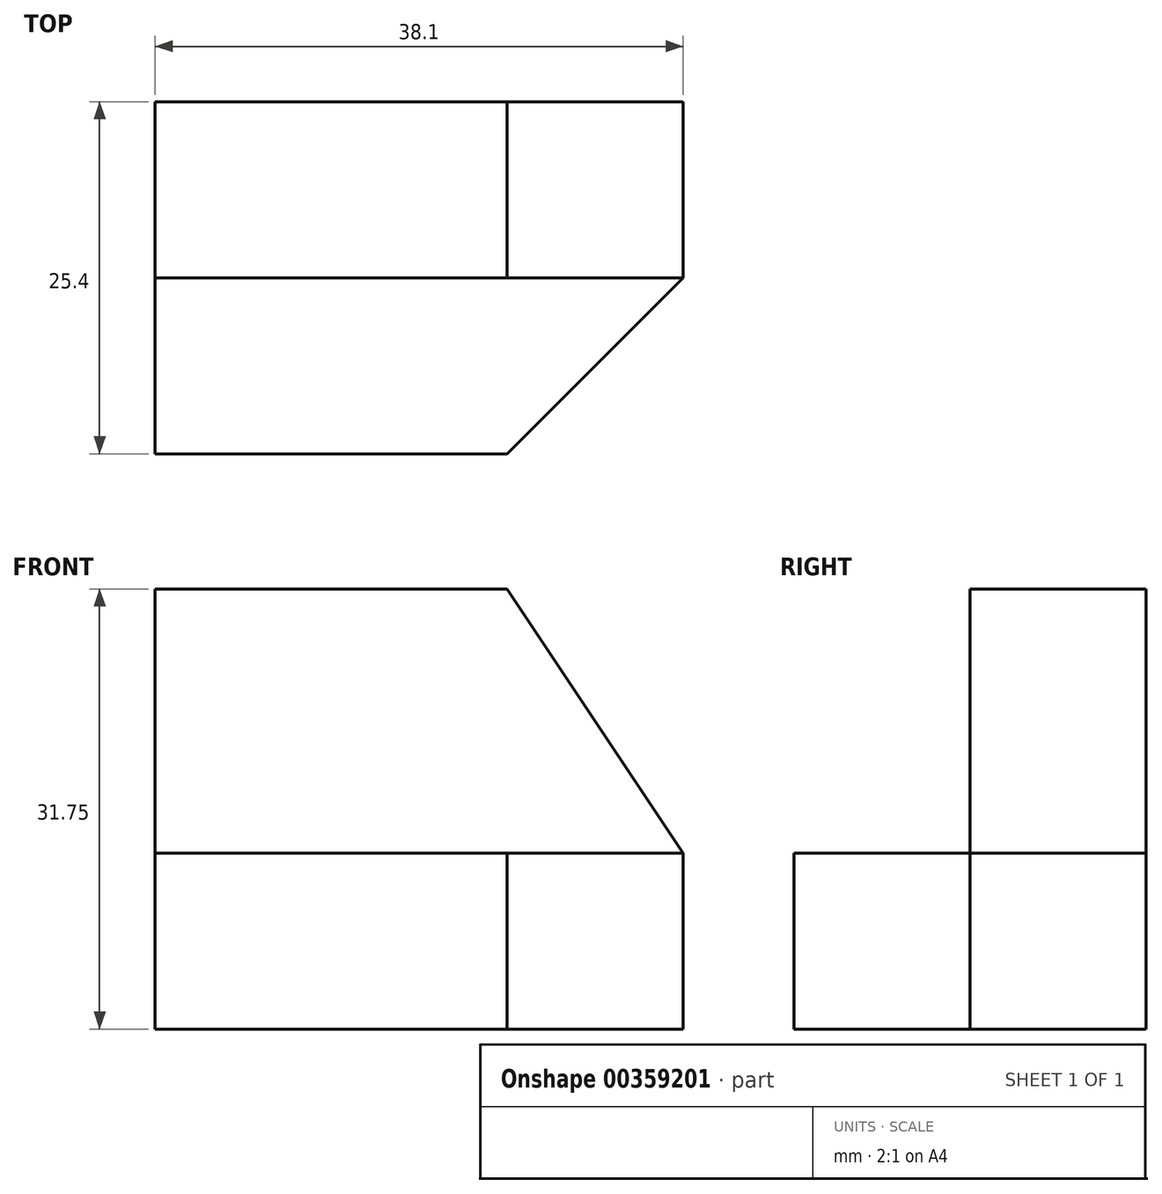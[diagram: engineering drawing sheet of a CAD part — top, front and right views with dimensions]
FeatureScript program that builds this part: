
annotation { "Feature Type Name" : "Feature", "Feature Type Description" : "" }
export const myFeature = defineFeature(function(context is Context, id is Id, definition is map)
    precondition{}
    {
        {
            var Q0;
            Q0=qCreatedBy(makeId("Right.planeOp"),FACE);
            var sketch = newSketch(context, id + "F0", { "sketchPlane" : qUnion([Q0])});
            skLineSegment(sketch, "E0", {"start": v(0, 0) * mm, "end": v(0, 12.7) * mm});
            skLineSegment(sketch, "E1", {"start": v(0, 12.7) * mm, "end": v(12.7, 12.7) * mm});
            skLineSegment(sketch, "E2", {"start": v(12.7, 12.7) * mm, "end": v(12.7, 31.75) * mm});
            skLineSegment(sketch, "E3", {"start": v(12.7, 31.75) * mm, "end": v(25.4, 31.75) * mm});
            skLineSegment(sketch, "E4", {"start": v(25.4, 31.75) * mm, "end": v(25.4, 0) * mm});
            skLineSegment(sketch, "E5", {"start": v(25.4, 0) * mm, "end": v(0, 0) * mm});
            skSolve(sketch);
        }
        {
            var Q0;
            Q0 = qSketchRegion(id + "F0", true);
            extrude(context, id + "F1", {"entities" : qUnion([Q0]), "oppositeDirection" : true, "depth" : 38.1 * mm});
        }
        {
            var Q0;
            Q0=makeQuery(id+"F1.opExtrude","SWEPT_FACE",FACE,{"disambiguationData":[OSD([sQuery(id+"F0.wireOp",EDGE,"E2")])]});
            var sketch = newSketch(context, id + "F2", { "sketchPlane" : qUnion([Q0])});
            skLineSegment(sketch, "E6", {"start": v(-12.7, 31.75) * mm, "end": v(0, 12.7) * mm});
            skLineSegment(sketch, "E7", {"start": v(0, 12.7) * mm, "end": v(0, 31.75) * mm});
            skLineSegment(sketch, "E8", {"start": v(0, 31.75) * mm, "end": v(-12.7, 31.75) * mm});
            skSolve(sketch);
        }
        {
            var Q0;
            Q0 = qSketchRegion(id + "F2", true);
            extrude(context, id + "F3", {"entities" : qUnion([Q0]), "operationType" : NewBodyOperationType.REMOVE, "oppositeDirection" : true, "depth" : 25.4 * mm});
        }
        {
            var Q0;
            Q0=makeQuery(id+"F1.opExtrude","SWEPT_FACE",FACE,{"disambiguationData":[OSD([sQuery(id+"F0.wireOp",EDGE,"E1")])]});
            var sketch = newSketch(context, id + "F4", { "sketchPlane" : qUnion([Q0])});
            skLineSegment(sketch, "E9", {"start": v(0, 12.7) * mm, "end": v(-12.7, 0) * mm});
            skLineSegment(sketch, "E10", {"start": v(-12.7, 0) * mm, "end": v(0, 0) * mm});
            skLineSegment(sketch, "E11", {"start": v(0, 0) * mm, "end": v(0, 12.7) * mm});
            skSolve(sketch);
        }
        {
            var Q0;
            Q0 = qSketchRegion(id + "F4", true);
            extrude(context, id + "F5", {"entities" : qUnion([Q0]), "operationType" : NewBodyOperationType.REMOVE, "oppositeDirection" : true, "depth" : 25.4 * mm});
        }
    });
